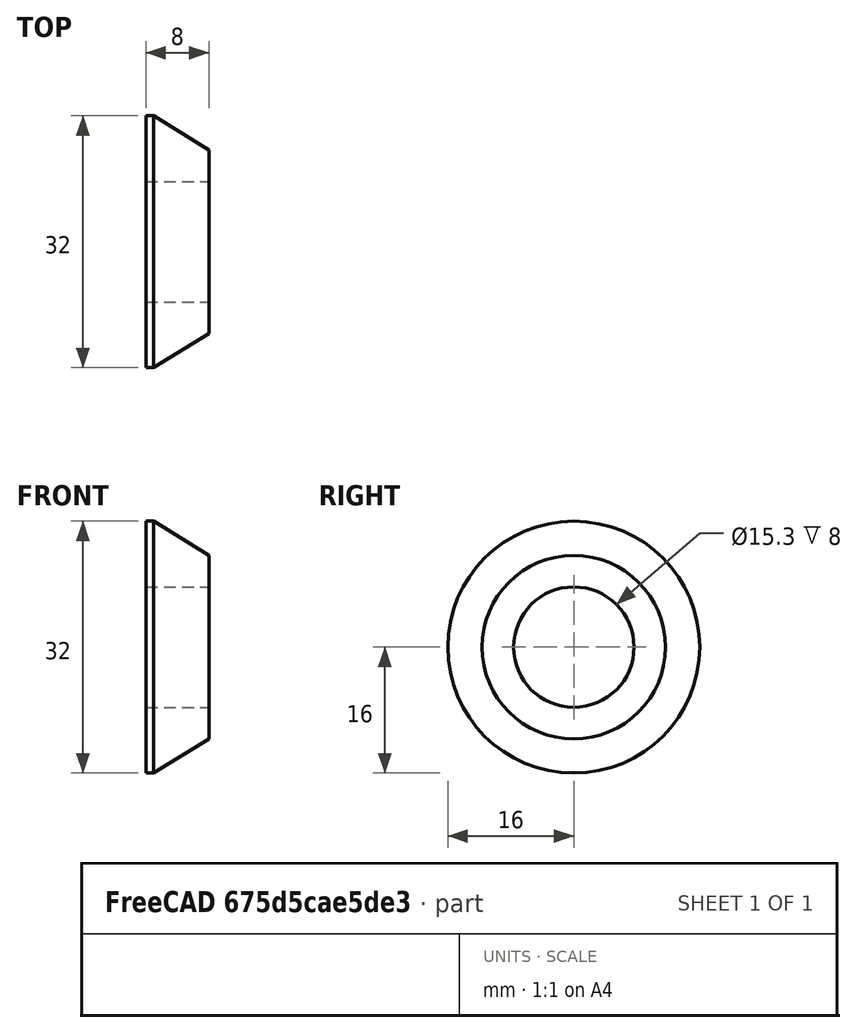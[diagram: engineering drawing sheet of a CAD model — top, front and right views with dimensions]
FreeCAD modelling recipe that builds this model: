
FCSTD DOCUMENT  (FreeCAD 0.16R)
Label: DustSpacer
License: All rights reserved
LicenseURL: http://en.wikipedia.org/wiki/All_rights_reserved
objects: Sketcher::SketchObject×1, PartDesign::Revolution×1, Mesh::Feature×1
note: 3 computed .brp shape members not serialized (recipe doc carries the construction recipe); baked Part::Feature solids carry a one-line shape summary decoded from their .brp

FEATURE [Sketcher::SketchObject] Sketch
  sketch-geometry (5):
    g0: LineSegment StartX=-5.3972 StartY=7.65 StartZ=0 EndX=2.6028 EndY=7.65 EndZ=0
    g1: LineSegment StartX=2.6028 StartY=7.65 StartZ=0 EndX=2.6028 EndY=11.65 EndZ=0
    g2: LineSegment StartX=2.6028 StartY=11.65 StartZ=0 EndX=-4.3972 EndY=16 EndZ=0
    g3: LineSegment StartX=-5.3972 StartY=16 StartZ=0 EndX=-5.3972 EndY=7.65 EndZ=0
    g4: LineSegment StartX=-5.3972 StartY=16 StartZ=0 EndX=-4.3972 EndY=16 EndZ=0
  constraints (14):
    c: Horizontal(g0)
    c: Coincident(g0,g1)
    c: Coincident(g1,g2)
    c: Vertical(g3)
    c: Coincident(g0,g3)
    c: DistanceY(g2) = 16
    c: DistanceY(g0) = 7.65
    c: Distance(g0) = 8
    c: Vertical(g1)
    c: Distance(g1) = 4
    c: Horizontal(g4)
    c: Coincident(g4,g3)
    c: Coincident(g4,g2)
    c: Distance(g4) = 1
FEATURE [PartDesign::Revolution] Revolution
  Angle = 360
  Axis = (1,0,0)
  Base = (0,0,0)
  ReferenceAxis = -> Sketch [H_Axis]
  Sketch = -> Sketch
FEATURE [Mesh::Feature] Mesh  label="Revolution (Meshed)"
